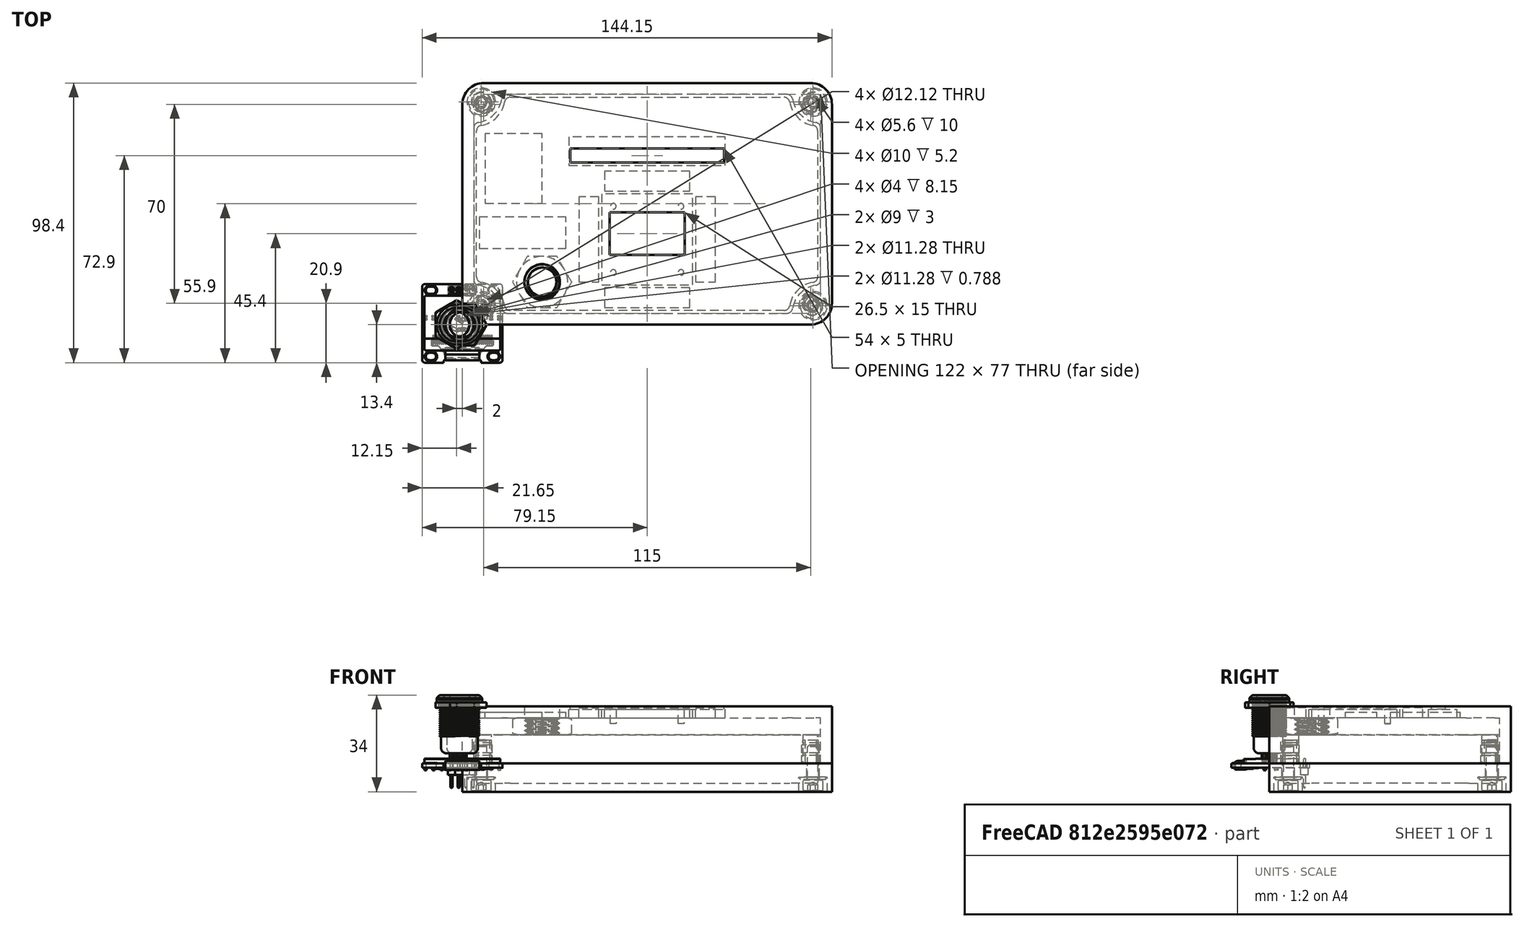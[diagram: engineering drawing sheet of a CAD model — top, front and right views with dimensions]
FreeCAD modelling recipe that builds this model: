
FCSTD DOCUMENT  (FreeCAD 0.20R27319 (Git))
Label: FirstDraft
License: All rights reserved
LicenseURL: http://en.wikipedia.org/wiki/All_rights_reserved
objects: Part::Feature×49, Part::FeaturePython×14, Sketcher::SketchObject×12, App::Part×10, PartDesign::Pocket×7, PartDesign::CoordinateSystem×4, App::DocumentObjectGroup×4, PartDesign::Line×4, PartDesign::Pad×3, App::Link×2, PartDesign::Body×2, PartDesign::AdditiveBox×1, Mesh::Feature×1, App::FeaturePython×1, PartDesign::Fillet×1, PartDesign::ShapeBinder×1, PartDesign::Hole×1
note: 112 computed .brp shape members not serialized (recipe doc carries the construction recipe); baked Part::Feature solids carry a one-line shape summary decoded from their .brp

FEATURE [PartDesign::AdditiveBox] Box002
  AttacherType = Attacher::AttachEngine3D
  Height = 20
  Length = 130
  Width = 85
FEATURE [Sketcher::SketchObject] Sketch001
  ExternalGeometry = -> [Box002]
  FullyConstrained = true
  MapMode = 5
  Placement = pos=(0,0,0) rot=(1,0,0;3.14159rad)
  Support = -> [Box002]
  sketch-geometry (23):
    g0: LineSegment StartX=15.8322 StartY=-4 StartZ=0 EndX=114.168 EndY=-4 EndZ=0
    g1: LineSegment StartX=126 StartY=-15.8322 StartZ=0 EndX=126 EndY=-69.1678 EndZ=0
    g2: LineSegment StartX=114.168 StartY=-81 StartZ=0 EndX=15.8322 EndY=-81 EndZ=0
    g3: LineSegment StartX=4 StartY=-69.1678 StartZ=0 EndX=4 EndY=-15.8322 EndZ=0
    g4: GeomPoint X=4 Y=-4 Z=0
    g5: GeomPoint X=126 Y=-81 Z=0
    g6: GeomPoint X=65 Y=-42.5 Z=0
    g7: ArcOfCircle CenterX=4 CenterY=-81 CenterZ=0 NormalX=0 NormalY=0 NormalZ=1 AngleXU=0 Radius=10 StartAngle=0.167448 EndAngle=1.40335
    g8: ArcOfCircle CenterX=6 CenterY=-69.1678 CenterZ=0 NormalX=0 NormalY=0 NormalZ=1 AngleXU=0 Radius=2 StartAngle=3.14159 EndAngle=4.54494
    g9: ArcOfCircle CenterX=15.8322 CenterY=-79 CenterZ=0 NormalX=0 NormalY=0 NormalZ=1 AngleXU=0 Radius=2 StartAngle=3.30904 EndAngle=4.71239
    g10: ArcOfCircle CenterX=4 CenterY=-4 CenterZ=0 NormalX=0 NormalY=0 NormalZ=1 AngleXU=0 Radius=10 StartAngle=4.87984 EndAngle=6.11574
    g11: ArcOfCircle CenterX=126 CenterY=-4 CenterZ=0 NormalX=0 NormalY=0 NormalZ=1 AngleXU=0 Radius=10 StartAngle=3.30904 EndAngle=4.54494
    g12: ArcOfCircle CenterX=126 CenterY=-81 CenterZ=0 NormalX=0 NormalY=0 NormalZ=1 AngleXU=0 Radius=10 StartAngle=1.73824 EndAngle=2.97414
    g13: LineSegment StartX=4 StartY=-81 StartZ=0 EndX=126 EndY=-81 EndZ=0
    g14: LineSegment StartX=126 StartY=-81 StartZ=0 EndX=126 EndY=-4 EndZ=0
    g15: LineSegment StartX=126 StartY=-4 StartZ=0 EndX=4 EndY=-4 EndZ=0
    g16: LineSegment StartX=4 StartY=-4 StartZ=0 EndX=4 EndY=-81 EndZ=0
    g17: ArcOfCircle CenterX=6 CenterY=-15.8322 CenterZ=0 NormalX=0 NormalY=0 NormalZ=1 AngleXU=0 Radius=2 StartAngle=1.73824 EndAngle=3.14159
    g18: ArcOfCircle CenterX=124 CenterY=-15.8322 CenterZ=0 NormalX=0 NormalY=0 NormalZ=1 AngleXU=0 Radius=2 StartAngle=0 EndAngle=1.40335
    g19: ArcOfCircle CenterX=15.8322 CenterY=-6 CenterZ=0 NormalX=0 NormalY=0 NormalZ=1 AngleXU=0 Radius=2 StartAngle=1.5708 EndAngle=2.97414
    g20: ArcOfCircle CenterX=114.168 CenterY=-6 CenterZ=0 NormalX=0 NormalY=0 NormalZ=1 AngleXU=0 Radius=2 StartAngle=0.167448 EndAngle=1.5708
    g21: ArcOfCircle CenterX=124 CenterY=-69.1678 CenterZ=0 NormalX=0 NormalY=0 NormalZ=1 AngleXU=0 Radius=2 StartAngle=4.87984 EndAngle=6.28319
    g22: ArcOfCircle CenterX=114.168 CenterY=-79 CenterZ=0 NormalX=0 NormalY=0 NormalZ=1 AngleXU=0 Radius=2 StartAngle=4.71239 EndAngle=6.11574
  constraints (56):
    c: Horizontal(g0)
    c: Horizontal(g2)
    c: Vertical(g1)
    c: Vertical(g3)
    c: PointOnObject(g4,g0)
    c: PointOnObject(g4,g3)
    c: PointOnObject(g5,g1)
    c: PointOnObject(g5,g2)
    c: Symmetric(g-6,g-4,g6)
    c: Tangent(g7,g8) = 1.5708
    c: Tangent(g3,g8) = 1.5708
    c: Tangent(g2,g9) = 1.5708
    c: Tangent(g7,g9) = 1.5708
    c: Coincident(g12,g5)
    c: Coincident(g13,g14)
    c: Coincident(g14,g15)
    c: Coincident(g15,g16)
    c: Coincident(g16,g13)
    c: Horizontal(g13)
    c: Horizontal(g15)
    c: Vertical(g14)
    c: Vertical(g16)
    c: Coincident(g13,g7)
    c: Coincident(g14,g11)
    c: Coincident(g4,g10)
    c: Symmetric(g7,g11,g6)
    c: Tangent(g3,g17) = 1.5708
    c: Tangent(g10,g17) = 1.5708
    c: Tangent(g1,g18) = 1.5708
    c: Tangent(g11,g18) = 1.5708
    c: Tangent(g10,g19) = 1.5708
    c: Tangent(g0,g19) = 1.5708
    c: Tangent(g11,g20) = 1.5708
    c: Tangent(g0,g20) = 1.5708
    c: Tangent(g1,g21) = 1.5708
    c: Tangent(g12,g21) = 1.5708
    c: Tangent(g2,g22) = 1.5708
    c: Tangent(g12,g22) = 1.5708
    c: PointOnObject(g0,g15)
    c: PointOnObject(g3,g16)
    c: PointOnObject(g1,g14)
    c: DistanceX(g-6,g7) = 4
    c: DistanceY(g-6,g7) = 4
    c: PointOnObject(g2,g13)
    c: Equal(g7,g10)
    c: Equal(g10,g11)
    c: Equal(g11,g12)
    c: Radius(g7) = 10
    c: Equal(g9,g8)
    c: Equal(g8,g19)
    c: Equal(g19,g17)
    c: Equal(g17,g20)
    c: Equal(g20,g18)
    c: Equal(g18,g21)
    c: Equal(g21,g22)
    c: Radius(g9) = 2
FEATURE [PartDesign::Pocket] Pocket001
  BaseFeature = -> Box002
  Direction = (0,0,1)
  Length = 16
  Length2 = 100
  Profile = -> Sketch001
  ReferenceAxis = -> Sketch001 [N_Axis]
  Type = 0
  expr: Length = <<Box002>>.Height - 4mm
FEATURE [Sketcher::SketchObject] Sketch002
  ExternalGeometry = -> [Pocket001]
  FullyConstrained = true
  MapMode = 5
  Placement = pos=(0,0,16) rot=(1,0,0;3.14159rad)
  Support = -> [Pocket001]
  sketch-geometry (11):
    g0: LineSegment StartX=49 StartY=-14 StartZ=0 EndX=81 EndY=-14 EndZ=0
    g1: LineSegment StartX=81 StartY=-14 StartZ=0 EndX=81 EndY=-46 EndZ=0
    g2: LineSegment StartX=81 StartY=-46 StartZ=0 EndX=49 EndY=-46 EndZ=0
    g3: LineSegment StartX=49 StartY=-46 StartZ=0 EndX=49 EndY=-14 EndZ=0
    g4: GeomPoint X=65 Y=-4 Z=0
    g5: LineSegment StartX=65 StartY=-4 StartZ=0 EndX=65 EndY=-14 EndZ=0
    g6: LineSegment StartX=37.5 StartY=-56 StartZ=0 EndX=92.5 EndY=-56 EndZ=0
    g7: LineSegment StartX=92.5 StartY=-56 StartZ=0 EndX=92.5 EndY=-66 EndZ=0
    g8: LineSegment StartX=92.5 StartY=-66 StartZ=0 EndX=37.5 EndY=-66 EndZ=0
    g9: LineSegment StartX=37.5 StartY=-66 StartZ=0 EndX=37.5 EndY=-56 EndZ=0
    g10: LineSegment StartX=65 StartY=-14 StartZ=0 EndX=65 EndY=-56 EndZ=0
  constraints (29):
    c: Coincident(g0,g1)
    c: Coincident(g1,g2)
    c: Coincident(g2,g3)
    c: Coincident(g3,g0)
    c: Horizontal(g0)
    c: Horizontal(g2)
    c: Vertical(g1)
    c: Vertical(g3)
    c: Coincident(g5,g4)
    c: Vertical(g5)
    c: Symmetric(g0,g0,g5)
    c: DistanceY(g5,g5) = 10
    c: DistanceY(g1,g1) = 32
    c: Equal(g1,g0)
    c: Coincident(g6,g7)
    c: Coincident(g7,g8)
    c: Coincident(g8,g9)
    c: Coincident(g9,g6)
    c: Horizontal(g6)
    c: Horizontal(g8)
    c: Vertical(g7)
    c: Vertical(g9)
    c: DistanceX(g6,g6) = 55
    c: DistanceY(g7,g7) = 10
    c: Coincident(g10,g5)
    c: Vertical(g10)
    c: Symmetric(g6,g6,g10)
    c: DistanceY(g6,g1) = 10
    c: Symmetric(g-3,g-3,g4)
FEATURE [PartDesign::Pocket] Pocket002  label="Platz OLED und LED-Strip"
  BaseFeature = -> Pocket001
  Direction = (0,0,1)
  Length = 3
  Length2 = 100
  Profile = -> Sketch002
  Type = 0
FEATURE [Sketcher::SketchObject] Sketch003
  ExternalGeometry = -> [Sketch002,Pocket002]
  FullyConstrained = true
  MapMode = 5
  Placement = pos=(0,0,16) rot=(1,0,0;3.14159rad)
  Support = -> [Pocket002]
  sketch-geometry (10):
    g0: LineSegment StartX=51.75 StartY=-24.5 StartZ=0 EndX=78.25 EndY=-24.5 EndZ=0
    g1: LineSegment StartX=78.25 StartY=-24.5 StartZ=0 EndX=78.25 EndY=-39.5 EndZ=0
    g2: LineSegment StartX=78.25 StartY=-39.5 StartZ=0 EndX=51.75 EndY=-39.5 EndZ=0
    g3: LineSegment StartX=51.75 StartY=-39.5 StartZ=0 EndX=51.75 EndY=-24.5 EndZ=0
    g4: LineSegment StartX=38 StartY=-57 StartZ=0 EndX=92 EndY=-57 EndZ=0
    g5: LineSegment StartX=92 StartY=-57 StartZ=0 EndX=92 EndY=-62 EndZ=0
    g6: LineSegment StartX=92 StartY=-62 StartZ=0 EndX=38 EndY=-62 EndZ=0
    g7: LineSegment StartX=38 StartY=-62 StartZ=0 EndX=38 EndY=-57 EndZ=0
    g8: LineSegment StartX=65 StartY=-57 StartZ=0 EndX=65 EndY=-56 EndZ=0
    g9: LineSegment StartX=65 StartY=-24.5 StartZ=0 EndX=65 EndY=-14 EndZ=0
  constraints (28):
    c: Coincident(g0,g1)
    c: Coincident(g1,g2)
    c: Coincident(g2,g3)
    c: Coincident(g3,g0)
    c: Horizontal(g0)
    c: Horizontal(g2)
    c: Vertical(g1)
    c: Vertical(g3)
    c: DistanceX(g0,g0) = 26.5
    c: DistanceY(g1,g1) = 15
    c: Coincident(g4,g5)
    c: Coincident(g5,g6)
    c: Coincident(g6,g7)
    c: Coincident(g7,g4)
    c: Horizontal(g4)
    c: Horizontal(g6)
    c: Vertical(g5)
    c: Vertical(g7)
    c: DistanceX(g4,g-3) = 0.5
    c: Vertical(g8)
    c: Symmetric(g4,g4,g8)
    c: Symmetric(g-3,g-4,g8)
    c: DistanceY(g5,g5) = 5
    c: DistanceY(g4,g-3) = 1
    c: Vertical(g9)
    c: Symmetric(g0,g0,g9)
    c: DistanceY(g9,g9) = 10.5
    c: Symmetric(g-5,g-5,g9)
FEATURE [PartDesign::Pocket] Pocket003  label="Sichtausschnitt"
  BaseFeature = -> Pocket002
  Direction = (0,0,1)
  Length = 1.01
  Length2 = 100
  Profile = -> Sketch003
  ReferenceAxis = -> Sketch003 [N_Axis]
  Type = 1
FEATURE [Sketcher::SketchObject] Sketch004  label="Sketch Halter OLED"
  ExternalGeometry = -> [Sketch002]
  FullyConstrained = true
  MapMode = 5
  Placement = pos=(0,0,19) rot=(1,0,0;3.14159rad)
  Support = -> [Pocket003]
  sketch-geometry (9):
    g0: Circle CenterX=53.1 CenterY=-18.35 CenterZ=0 NormalX=0 NormalY=0 NormalZ=1 AngleXU=0 Radius=1
    g1: Circle CenterX=76.9 CenterY=-18.35 CenterZ=0 NormalX=0 NormalY=0 NormalZ=1 AngleXU=0 Radius=1
    g2: Circle CenterX=76.9 CenterY=-41.65 CenterZ=0 NormalX=0 NormalY=0 NormalZ=1 AngleXU=0 Radius=1
    g3: Circle CenterX=53.1 CenterY=-41.65 CenterZ=0 NormalX=0 NormalY=0 NormalZ=1 AngleXU=0 Radius=1
    g4: LineSegment StartX=53.1 StartY=-18.35 StartZ=0 EndX=76.9 EndY=-18.35 EndZ=0
    g5: LineSegment StartX=76.9 StartY=-18.35 StartZ=0 EndX=76.9 EndY=-41.65 EndZ=0
    g6: LineSegment StartX=76.9 StartY=-41.65 StartZ=0 EndX=53.1 EndY=-41.65 EndZ=0
    g7: LineSegment StartX=53.1 StartY=-41.65 StartZ=0 EndX=53.1 EndY=-18.35 EndZ=0
    g8: GeomPoint X=65 Y=-30 Z=0
  constraints (20):
    c: Coincident(g4,g5)
    c: Coincident(g5,g6)
    c: Coincident(g6,g7)
    c: Coincident(g7,g4)
    c: Horizontal(g4)
    c: Horizontal(g6)
    c: Vertical(g5)
    c: Vertical(g7)
    c: Coincident(g4,g0)
    c: Coincident(g5,g2)
    c: Coincident(g1,g4)
    c: Coincident(g3,g6)
    c: Equal(g0,g1)
    c: Equal(g1,g2)
    c: Equal(g2,g3)
    c: Diameter(g1) = 2
    c: DistanceX(g4,g4) = 23.8
    c: DistanceY(g5,g5) = 23.3
    c: Symmetric(g-4,g-6,g8)
    c: Symmetric(g3,g1,g8)
FEATURE [PartDesign::Pad] Pad  label="Halter OLED"
  BaseFeature = -> Pocket003
  Direction = (0,0,-1)
  Length = 5
  Length2 = 100
  Profile = -> Sketch004
  ReferenceAxis = -> Sketch004 [N_Axis]
  Type = 0
FEATURE [Sketcher::SketchObject] Sketch005
  ExternalGeometry = -> [Sketch002]
  FullyConstrained = true
  MapMode = 5
  Placement = pos=(0,0,16) rot=(1,0,0;3.14159rad)
  Support = -> [Pad]
  sketch-geometry (26):
    g0: LineSegment StartX=50 StartY=-6 StartZ=0 EndX=80 EndY=-6 EndZ=0
    g1: LineSegment StartX=80 StartY=-6 StartZ=0 EndX=80 EndY=-13 EndZ=0
    g2: LineSegment StartX=80 StartY=-13 StartZ=0 EndX=50 EndY=-13 EndZ=0
    g3: LineSegment StartX=50 StartY=-13 StartZ=0 EndX=50 EndY=-6 EndZ=0
    g4: LineSegment StartX=82 StartY=-15 StartZ=0 EndX=89 EndY=-15 EndZ=0
    g5: LineSegment StartX=89 StartY=-15 StartZ=0 EndX=89 EndY=-45 EndZ=0
    g6: LineSegment StartX=89 StartY=-45 StartZ=0 EndX=82 EndY=-45 EndZ=0
    g7: LineSegment StartX=82 StartY=-45 StartZ=0 EndX=82 EndY=-15 EndZ=0
    g8: LineSegment StartX=41 StartY=-15 StartZ=0 EndX=48 EndY=-15 EndZ=0
    g9: LineSegment StartX=48 StartY=-15 StartZ=0 EndX=48 EndY=-45 EndZ=0
    g10: LineSegment StartX=48 StartY=-45 StartZ=0 EndX=41 EndY=-45 EndZ=0
    g11: LineSegment StartX=41 StartY=-45 StartZ=0 EndX=41 EndY=-15 EndZ=0
    g12: LineSegment StartX=50 StartY=-47 StartZ=0 EndX=80 EndY=-47 EndZ=0
    g13: LineSegment StartX=80 StartY=-47 StartZ=0 EndX=80 EndY=-54 EndZ=0
    g14: LineSegment StartX=80 StartY=-54 StartZ=0 EndX=50 EndY=-54 EndZ=0
    g15: LineSegment StartX=50 StartY=-54 StartZ=0 EndX=50 EndY=-47 EndZ=0
    g16: LineSegment StartX=48 StartY=-13 StartZ=0 EndX=82 EndY=-13 EndZ=0
    g17: LineSegment StartX=82 StartY=-13 StartZ=0 EndX=82 EndY=-47 EndZ=0
    g18: LineSegment StartX=82 StartY=-47 StartZ=0 EndX=48 EndY=-47 EndZ=0
    g19: LineSegment StartX=48 StartY=-47 StartZ=0 EndX=48 EndY=-13 EndZ=0
    g20: GeomPoint X=65 Y=-30 Z=0
    g21: GeomPoint X=48 Y=-30 Z=0
    g22: GeomPoint X=116 Y=-13 Z=0
    g23: GeomPoint X=82 Y=-30 Z=0
    g24: GeomPoint X=65 Y=-47 Z=0
    g25: GeomPoint X=65 Y=-13 Z=0
  constraints (61):
    c: Coincident(g0,g1)
    c: Coincident(g1,g2)
    c: Coincident(g2,g3)
    c: Coincident(g3,g0)
    c: Horizontal(g0)
    c: Horizontal(g2)
    c: Vertical(g1)
    c: Vertical(g3)
    c: Coincident(g4,g5)
    c: Coincident(g5,g6)
    c: Coincident(g6,g7)
    c: Coincident(g7,g4)
    c: Horizontal(g4)
    c: Horizontal(g6)
    c: Vertical(g5)
    c: Vertical(g7)
    c: Coincident(g8,g9)
    c: Coincident(g9,g10)
    c: Coincident(g10,g11)
    c: Coincident(g11,g8)
    c: Horizontal(g8)
    c: Horizontal(g10)
    c: Vertical(g9)
    c: Vertical(g11)
    c: Coincident(g12,g13)
    c: Coincident(g13,g14)
    c: Coincident(g14,g15)
    c: Coincident(g15,g12)
    c: Horizontal(g12)
    c: Horizontal(g14)
    c: Vertical(g13)
    c: Vertical(g15)
    c: Equal(g4,g1)
    c: Equal(g1,g8)
    c: Equal(g8,g13)
    c: Coincident(g16,g17)
    c: Coincident(g17,g18)
    c: Coincident(g18,g19)
    c: Coincident(g19,g16)
    c: DistanceX(g-4,g16) = 1
    c: DistanceY(g-4,g16) = 1
    c: Symmetric(g16,g18,g20)
    c: Symmetric(g-6,g-4,g20)
    c: DistanceY(g15,g15) = 7
    c: Vertical(g19)
    c: Horizontal(g16)
    c: PointOnObject(g12,g18)
    c: Vertical(g17)
    c: Equal(g0,g11)
    c: Equal(g11,g5)
    c: Equal(g5,g14)
    c: DistanceY(g11,g11) = 30
    c: Symmetric(g18,g17,g24)
    c: Symmetric(g6,g4,g23)
    c: Symmetric(g16,g22,g16)
    c: Symmetric(g16,g18,g21)
    c: Symmetric(g8,g9,g21)
    c: Symmetric(g17,g16,g23)
    c: Symmetric(g12,g12,g24)
    c: Symmetric(g2,g1,g25)
    c: Symmetric(g16,g16,g25)
FEATURE [PartDesign::Pocket] Pocket004  label="Ausschnitte  Touch"
  BaseFeature = -> Pad
  Direction = (0,0,1)
  Length = 3.5
  Length2 = 100
  Profile = -> Sketch005
  Type = 0
FEATURE [Part::Feature] Part__Feature  label="Pantalla"
  Placement = pos=(4e-15,0.525,-1e-15) rot=(0,0,1;0rad)
  shape: bbox 26.68 x 19.2 x 1.6 mm, 12 faces (baked)
FEATURE [Part::Feature] Part__Feature001  label="PADS"
  shape: bbox 0.4 x 3 x 0.1 mm, 6 faces (baked)
FEATURE [Part::Feature] Part__Feature002  label="PADS001"
  shape: bbox 0.4 x 3 x 0.1 mm, 6 faces (baked)
FEATURE [Part::Feature] Part__Feature003  label="PADS002"
  shape: bbox 0.4 x 3 x 0.1 mm, 6 faces (baked)
FEATURE [Part::Feature] Part__Feature004  label="PADS003"
  shape: bbox 0.4 x 3 x 0.1 mm, 6 faces (baked)
FEATURE [Part::Feature] Part__Feature005  label="PADS004"
  shape: bbox 0.4 x 3 x 0.1 mm, 6 faces (baked)
FEATURE [Part::Feature] Part__Feature006  label="PADS005"
  shape: bbox 0.4 x 3 x 0.1 mm, 6 faces (baked)
FEATURE [Part::Feature] Part__Feature007  label="PADS006"
  shape: bbox 0.4 x 3 x 0.1 mm, 6 faces (baked)
FEATURE [Part::Feature] Part__Feature008  label="PADS007"
  shape: bbox 0.4 x 3 x 0.1 mm, 6 faces (baked)
FEATURE [Part::Feature] Part__Feature009  label="PADS008"
  shape: bbox 0.4 x 3 x 0.1 mm, 6 faces (baked)
FEATURE [Part::Feature] Part__Feature010  label="PADS009"
  shape: bbox 0.4 x 3 x 0.1 mm, 6 faces (baked)
FEATURE [Part::Feature] Part__Feature011  label="PADS010"
  shape: bbox 0.4 x 3 x 0.1 mm, 6 faces (baked)
FEATURE [Part::Feature] Part__Feature012  label="PADS011"
  shape: bbox 0.4 x 3 x 0.1 mm, 6 faces (baked)
FEATURE [Part::Feature] Part__Feature013  label="PADS012"
  shape: bbox 0.4 x 3 x 0.1 mm, 6 faces (baked)
FEATURE [Part::Feature] Part__Feature014  label="PADS013"
  shape: bbox 0.4 x 3 x 0.1 mm, 6 faces (baked)
FEATURE [Part::Feature] Part__Feature015  label="PADS014"
  shape: bbox 0.4 x 3 x 0.1 mm, 6 faces (baked)
FEATURE [Part::Feature] Part__Feature016  label="PADS015"
  shape: bbox 0.4 x 3 x 0.1 mm, 6 faces (baked)
FEATURE [Part::Feature] Part__Feature017  label="PADS016"
  shape: bbox 0.4 x 3 x 0.1 mm, 6 faces (baked)
FEATURE [Part::Feature] Part__Feature018  label="PADS017"
  shape: bbox 0.4 x 3 x 0.1 mm, 6 faces (baked)
FEATURE [Part::Feature] Part__Feature019  label="PADS018"
  shape: bbox 0.4 x 3 x 0.1 mm, 6 faces (baked)
FEATURE [Part::Feature] Part__Feature020  label="PADS019"
  shape: bbox 0.4 x 3 x 0.1 mm, 6 faces (baked)
FEATURE [Part::Feature] Part__Feature021  label="PADS020"
  shape: bbox 0.4 x 3 x 0.1 mm, 6 faces (baked)
FEATURE [Part::Feature] Part__Feature022  label="PADS021"
  shape: bbox 0.4 x 3 x 0.1 mm, 6 faces (baked)
FEATURE [Part::Feature] Part__Feature023  label="PADS022"
  shape: bbox 0.4 x 3 x 0.1 mm, 6 faces (baked)
FEATURE [Part::Feature] Part__Feature024  label="PADS023"
  shape: bbox 0.4 x 3 x 0.1 mm, 6 faces (baked)
FEATURE [Part::Feature] Part__Feature025  label="PADS024"
  shape: bbox 0.4 x 3 x 0.1 mm, 6 faces (baked)
FEATURE [Part::Feature] Part__Feature026  label="PADS025"
  shape: bbox 0.4 x 3 x 0.1 mm, 6 faces (baked)
FEATURE [Part::Feature] Part__Feature027  label="PADS026"
  shape: bbox 0.4 x 3 x 0.1 mm, 6 faces (baked)
FEATURE [Part::Feature] Part__Feature028  label="PADS027"
  shape: bbox 0.4 x 3 x 0.1 mm, 6 faces (baked)
FEATURE [Part::Feature] Part__Feature029  label="PADS028"
  shape: bbox 0.4 x 3 x 0.1 mm, 6 faces (baked)
FEATURE [Part::Feature] Part__Feature030  label="PADS029"
  shape: bbox 0.4 x 3 x 0.1 mm, 6 faces (baked)
FEATURE [App::Part] PADS  label="PADS030"
  Group = -> [Part__Feature001,Part__Feature002,Part__Feature003,Part__Feature004,Part__Feature005,Part__Feature006,Part__Feature007,Part__Feature008,Part__Feature009,Part__Feature010,Part__Feature011,Part__Feature012,Part__Feature013,Part__Feature014,Part__Feature015,Part__Feature016,Part__Feature017,Part__Feature018,Part__Feature019,Part__Feature020,Part__Feature021,Part__Feature022,Part__Feature023,+7 more]
  Origin = -> Origin005
FEATURE [Part::Feature] Part__Feature031  label="Base PCB"
  shape: bbox 28.3 x 27.65 x 1.7 mm, 324 faces (baked)
FEATURE [App::Part] Base_PCB  label="Base PCB001"
  Group = -> [PADS,Part__Feature031]
  Origin = -> Origin006
FEATURE [Part::Feature] Part__Feature032  label="PINOS"
  shape: bbox 2.54 x 2.54 x 10.4 mm, 28 faces (baked)
FEATURE [Part::Feature] Part__Feature033  label="PINOS001"
  shape: bbox 2.54 x 2.54 x 10.4 mm, 28 faces (baked)
FEATURE [Part::Feature] Part__Feature034  label="PINOS002"
  shape: bbox 2.54 x 2.54 x 10.4 mm, 28 faces (baked)
FEATURE [Part::Feature] Part__Feature035  label="PINOS003"
  shape: bbox 2.54 x 2.54 x 10.4 mm, 28 faces (baked)
FEATURE [App::Part] PINOS  label="PINOS004"
  Group = -> [Part__Feature032,Part__Feature033,Part__Feature034,Part__Feature035]
  Origin = -> Origin007
FEATURE [Part::Feature] Part__Feature036  label="fLEX"
  Placement = pos=(4e-15,1.525,-0.1) rot=(0,0,1;0rad)
  shape: bbox 39.56 x 36.02 x 13.34 mm, 31 faces (baked)
FEATURE [Part::Feature] Part__Feature037  label="res"
  Placement = pos=(13,2.425,-4) rot=(1,0,0;3.14159rad)
  shape: bbox 1.02 x 1.65 x 0.81 mm, 37 faces (baked)
FEATURE [Part::Feature] Part__Feature038  label="res001"
  Placement = pos=(10.1111,2.425,-4) rot=(1,0,0;3.14159rad)
  shape: bbox 1.02 x 1.65 x 0.81 mm, 37 faces (baked)
FEATURE [Part::Feature] Part__Feature039  label="res002"
  Placement = pos=(7.22222,2.425,-4) rot=(1,0,0;3.14159rad)
  shape: bbox 1.02 x 1.65 x 0.81 mm, 37 faces (baked)
FEATURE [Part::Feature] Part__Feature040  label="res003"
  Placement = pos=(4.33333,2.425,-4) rot=(1,0,0;3.14159rad)
  shape: bbox 1.02 x 1.65 x 0.81 mm, 37 faces (baked)
FEATURE [Part::Feature] Part__Feature041  label="res004"
  Placement = pos=(1.44444,2.425,-4) rot=(1,0,0;3.14159rad)
  shape: bbox 1.02 x 1.65 x 0.81 mm, 37 faces (baked)
FEATURE [Part::Feature] Part__Feature042  label="res005"
  Placement = pos=(-1.44444,2.425,-4) rot=(1,0,0;3.14159rad)
  shape: bbox 1.02 x 1.65 x 0.81 mm, 37 faces (baked)
FEATURE [Part::Feature] Part__Feature043  label="res006"
  Placement = pos=(-4.33333,2.425,-4) rot=(1,0,0;3.14159rad)
  shape: bbox 1.02 x 1.65 x 0.81 mm, 37 faces (baked)
FEATURE [Part::Feature] Part__Feature044  label="res007"
  Placement = pos=(-7.22222,2.425,-4) rot=(1,0,0;3.14159rad)
  shape: bbox 1.02 x 1.65 x 0.81 mm, 37 faces (baked)
FEATURE [Part::Feature] Part__Feature045  label="res008"
  Placement = pos=(-10.1111,2.425,-4) rot=(1,0,0;3.14159rad)
  shape: bbox 1.02 x 1.65 x 0.81 mm, 37 faces (baked)
FEATURE [Part::Feature] Part__Feature046  label="res009"
  Placement = pos=(-13,2.425,-4) rot=(1,0,0;3.14159rad)
  shape: bbox 1.02 x 1.65 x 0.81 mm, 37 faces (baked)
FEATURE [Part::Feature] Part__Feature047  label="res010"
  Placement = pos=(0,-1.575,-4) rot=(0.707107,-0.707107,0;3.14159rad)
  shape: bbox 1.65 x 1.02 x 0.81 mm, 37 faces (baked)
FEATURE [App::Part] Resistores_SMD  label="Resistores SMD"
  Group = -> [Part__Feature037,Part__Feature038,Part__Feature039,Part__Feature040,Part__Feature041,Part__Feature042,Part__Feature043,Part__Feature044,Part__Feature045,Part__Feature046,Part__Feature047]
  Origin = -> Origin008
FEATURE [App::Part] Tela_OLed_128x64_v15  label="Tela OLed 128x64 v15"
  Group = -> [Part__Feature,Base_PCB,PINOS,Part__Feature036,Resistores_SMD]
  Origin = -> Origin009
  Placement = pos=(60,29.5,22.5) rot=(0,0,1;0rad)
FEATURE [Mesh::Feature] DuinoPeak_WS2812_RGB_Pixel
FEATURE [Part::Feature] Part__Feature086  label="12mm Switch"
  shape: bbox 17.01 x 15.16 x 24 mm, 165 faces, 3 solids (baked)
FEATURE [App::Part] _2mm_Switch_v5  label="12mm Switch v5"
  Group = -> [Part__Feature086]
  Origin = -> Origin012
  Placement = pos=(15,0,0) rot=(1,0,0;0rad)
FEATURE [Part::FeaturePython] Clone  label="12mm Switch v006"  # Draft clone (typed FeaturePython)
  AttacherType = Attacher::AttachEngine3D
  Fuse = false
  Objects = -> [_2mm_Switch_v5]
  Placement = pos=(-2,-1e-15,0) rot=(0,0,-1;0.523599rad)
  Scale = (1,1,1)
FEATURE [PartDesign::CoordinateSystem] LCS_Origin
  AttacherType = Attacher::AttachEngine3D
  MapMode = 2
  Support = -> [X_Axis013]
FEATURE [App::FeaturePython] Variables  # WARN: FeaturePython — macro-defined, semantics opaque (R4)
  Type = App::PropertyContainer
FEATURE [App::DocumentObjectGroup] Constraints
FEATURE [App::DocumentObjectGroup] Configurations
FEATURE [App::Part] Part  label="Double-Switch"
  Group = -> [Clone,_2mm_Switch_v5]
  Origin = -> Origin014
FEATURE [App::Part] Part001  label="LED-Strip"
  Group = -> [DuinoPeak_WS2812_RGB_Pixel]
  Origin = -> Origin015
  Placement = pos=(34,56,20.6) rot=(0,0,1;0rad)
FEATURE [App::Link] Base  label="Base001"
  AssemblyType = Part::Link
  AttachedBy = #LCS_1
  AttachedTo = Parent Assembly#LCS_Origin
  LinkedObject = -> Body
  SolverId = Asm4EE
  expr: Placement = LCS_Origin.Placement * AttachmentOffset * LCS_1.Placement ^ -1
FEATURE [Part::FeaturePython] HeatSet  label="Auto-HeatSet"  # WARN: FeaturePython — macro-defined, semantics opaque (R4)
  Placement = pos=(7.5,77.5,0) rot=(-1,0,0;3.14159rad)
  baseObject = -> Pocket006 [Edge32]
  diameter = 0
  invert = false
  offset = 0
FEATURE [Part::FeaturePython] HeatSet001  label="Auto-HeatSet001"  # WARN: FeaturePython — macro-defined, semantics opaque (R4)
  Placement = pos=(122.5,77.5,0) rot=(-1,0,0;3.14159rad)
  baseObject = -> Pocket006 [Edge49]
  diameter = 0
  invert = false
  offset = 0
FEATURE [Part::FeaturePython] HeatSet002  label="Auto-HeatSet002"  # WARN: FeaturePython — macro-defined, semantics opaque (R4)
  Placement = pos=(122.5,7.5,0) rot=(-1,0,0;3.14159rad)
  baseObject = -> Pocket006 [Edge31]
  diameter = 0
  invert = false
  offset = 0
FEATURE [Part::FeaturePython] HeatSet003  label="Auto-HeatSet003"  # WARN: FeaturePython — macro-defined, semantics opaque (R4)
  Placement = pos=(7.5,7.5,0) rot=(-1,0,0;3.14159rad)
  baseObject = -> Body002 [Edge30]
  diameter = 0
  invert = false
  offset = 0
FEATURE [App::Link] Front_inkl__Fasteners  label="Front inkl. Fasteners001"
  AssemblyType = Part::Link
  AttachedBy = #LCS_3
  AttachedTo = Base#LCS_1
  LinkedObject = -> Part002
  SolverId = Asm4EE
  expr: Placement = Base.Placement * LCS_1.Placement * AttachmentOffset * LCS_3.Placement ^ -1
FEATURE [Part::FeaturePython] Washer  label="M4-Washer"  # Fasteners workbench fastener (typed FeaturePython)
  Placement = pos=(6.65146,6.65148,-4.8) rot=(-1,0,0;3.14159rad)
  baseObject = -> Body [Edge50]
  diameter = 5
  invert = false
  matchOuter = true
  offset = 0
  type = 3
FEATURE [Part::FeaturePython] Washer001  label="M4-Washer022"  # Fasteners workbench fastener (typed FeaturePython)
  Placement = pos=(123.349,6.65148,-4.8) rot=(-1,0,0;3.14159rad)
  baseObject = -> Body [Edge52]
  diameter = 5
  invert = false
  matchOuter = true
  offset = 0
  type = 3
FEATURE [Part::FeaturePython] Washer002  label="M4-Washer023"  # Fasteners workbench fastener (typed FeaturePython)
  Placement = pos=(123.349,78.3485,-4.8) rot=(-1,0,0;3.14159rad)
  baseObject = -> Body [Edge88]
  diameter = 5
  invert = false
  matchOuter = true
  offset = 0
  type = 3
FEATURE [Part::FeaturePython] Washer003  label="M4-Washer024"  # Fasteners workbench fastener (typed FeaturePython)
  Placement = pos=(6.65146,78.3485,-4.8) rot=(-1,0,0;3.14159rad)
  baseObject = -> Body [Edge54]
  diameter = 5
  invert = false
  matchOuter = true
  offset = 0
  type = 3
FEATURE [Part::FeaturePython] Screw  label="M4x14-Screw"  # Fasteners workbench fastener (typed FeaturePython)
  Placement = pos=(6.65146,78.3485,-5.7) rot=(-1,0,0;3.14159rad)
  baseObject = -> Washer003 [Edge1]
  diameter = 5
  invert = false
  length = 4
  lengthCustom = 14
  matchOuter = false
  offset = 0
  thread = false
  type = 34
FEATURE [Part::FeaturePython] Screw001  label="M4x12-Screw"  # Fasteners workbench fastener (typed FeaturePython)
  Placement = pos=(6.65146,6.65148,-5.7) rot=(-1,0,0;3.14159rad)
  baseObject = -> Washer [Edge1]
  diameter = 5
  invert = false
  length = 3
  lengthCustom = 12
  matchOuter = false
  offset = 0
  thread = false
  type = 34
FEATURE [Part::FeaturePython] Screw002  label="M4x12-Screw013"  # Fasteners workbench fastener (typed FeaturePython)
  Placement = pos=(123.349,6.65148,-5.7) rot=(-1,0,0;3.14159rad)
  baseObject = -> Washer001 [Edge1]
  diameter = 5
  invert = false
  length = 3
  lengthCustom = 12
  matchOuter = false
  offset = 0
  thread = false
  type = 34
FEATURE [Part::FeaturePython] Screw003  label="M4x12-Screw014"  # Fasteners workbench fastener (typed FeaturePython)
  Placement = pos=(123.349,78.3485,-5.7) rot=(-1,0,0;3.14159rad)
  baseObject = -> Washer002 [Edge1]
  diameter = 5
  invert = false
  length = 3
  lengthCustom = 12
  matchOuter = false
  offset = 0
  thread = false
  type = 34
FEATURE [App::DocumentObjectGroup] Fasteners
  Group = -> [Washer,Washer001,Washer002,Washer003,Screw,Screw001,Screw002,Screw003]
FEATURE [App::Part] Assembly
  AssemblyType = Part::Link
  Group = -> [LCS_Origin,Variables,Constraints,Configurations,Base,Front_inkl__Fasteners,Fasteners,Washer,Washer001,Washer002,Washer003,Screw,Screw001,Screw002,Screw003]
  Origin = -> Origin013
  Type = Assembly
FEATURE [PartDesign::Fillet] Fillet
  Base = -> Pocket004 [Edge3,Edge20,Edge6,Edge1]
  BaseFeature = -> Pocket004
  Radius = 7.5
  SupportTransform = false
FEATURE [Sketcher::SketchObject] Sketch
  ExternalGeometry = -> [Fillet]
  FullyConstrained = true
  MapMode = 5
  Placement = pos=(0,0,0) rot=(1,0,0;3.14159rad)
  Support = -> [Fillet]
  sketch-geometry (9):
    g0: LineSegment StartX=7.5 StartY=-7.5 StartZ=0 EndX=122.5 EndY=-7.5 EndZ=0
    g1: LineSegment StartX=122.5 StartY=-7.5 StartZ=0 EndX=122.5 EndY=-77.5 EndZ=0
    g2: LineSegment StartX=122.5 StartY=-77.5 StartZ=0 EndX=7.5 EndY=-77.5 EndZ=0
    g3: LineSegment StartX=7.5 StartY=-77.5 StartZ=0 EndX=7.5 EndY=-7.5 EndZ=0
    g4: GeomPoint X=65 Y=-42.5 Z=0
    g5: Circle CenterX=122.5 CenterY=-7.5 CenterZ=0 NormalX=0 NormalY=0 NormalZ=1 AngleXU=0 Radius=2.8
    g6: Circle CenterX=122.5 CenterY=-77.5 CenterZ=0 NormalX=0 NormalY=0 NormalZ=1 AngleXU=0 Radius=2.8
    g7: Circle CenterX=7.5 CenterY=-77.5 CenterZ=0 NormalX=0 NormalY=0 NormalZ=1 AngleXU=0 Radius=2.8
    g8: Circle CenterX=7.5 CenterY=-7.5 CenterZ=0 NormalX=0 NormalY=0 NormalZ=1 AngleXU=0 Radius=2.8
  constraints (19):
    c: Coincident(g0,g1)
    c: Coincident(g1,g2)
    c: Coincident(g2,g3)
    c: Coincident(g3,g0)
    c: Horizontal(g0)
    c: Horizontal(g2)
    c: Vertical(g1)
    c: Vertical(g3)
    c: Symmetric(g2,g0,g4)
    c: Coincident(g5,g0)
    c: Coincident(g6,g1)
    c: Coincident(g7,g2)
    c: Diameter(g7) = 5.6
    c: Equal(g5,g6)
    c: Equal(g6,g7)
    c: Equal(g7,g8)
    c: Symmetric(g-4,g-5,g4)
    c: Coincident(g0,g8)
    c: Coincident(g8,g-6)
FEATURE [PartDesign::Pocket] Pocket
  BaseFeature = -> Fillet
  Direction = (0,0,1)
  Length = 10
  Length2 = 5
  Profile = -> Sketch
  ReferenceAxis = -> Sketch [N_Axis]
  Type = 0
FEATURE [PartDesign::ShapeBinder] ShapeBinder
  Support = -> [Pocket]
  TraceSupport = true
FEATURE [Sketcher::SketchObject] Sketch010
  ExternalGeometry = -> [ShapeBinder]
  FullyConstrained = true
  MapMode = 5
  Placement = pos=(0,0,0) rot=(1,0,0;3.14159rad)
  Support = -> [ShapeBinder]
  sketch-geometry (23):
    g0: GeomPoint X=5 Y=-5 Z=0
    g1: GeomPoint X=125 Y=-80 Z=0
    g2: GeomPoint X=65 Y=-42.5 Z=0
    g3: ArcOfCircle CenterX=5 CenterY=-80 CenterZ=0 NormalX=0 NormalY=0 NormalZ=1 AngleXU=0 Radius=10 StartAngle=0.167448 EndAngle=1.40335
    g4: ArcOfCircle CenterX=7 CenterY=-68.1678 CenterZ=0 NormalX=0 NormalY=0 NormalZ=1 AngleXU=0 Radius=2 StartAngle=3.14159 EndAngle=4.54494
    g5: ArcOfCircle CenterX=5 CenterY=-5 CenterZ=0 NormalX=0 NormalY=0 NormalZ=1 AngleXU=0 Radius=10 StartAngle=1.40335 EndAngle=6.11574
    g6: ArcOfCircle CenterX=125 CenterY=-5 CenterZ=0 NormalX=0 NormalY=0 NormalZ=1 AngleXU=0 Radius=10 StartAngle=3.30904 EndAngle=4.54494
    g7: ArcOfCircle CenterX=125 CenterY=-80 CenterZ=0 NormalX=0 NormalY=0 NormalZ=1 AngleXU=0 Radius=10 StartAngle=1.73824 EndAngle=2.97414
    g8: LineSegment StartX=5 StartY=-80 StartZ=0 EndX=125 EndY=-80 EndZ=0
    g9: LineSegment StartX=125 StartY=-80 StartZ=0 EndX=125 EndY=-5 EndZ=0
    g10: LineSegment StartX=5 StartY=-5 StartZ=0 EndX=5 EndY=-80 EndZ=0
    g11: ArcOfCircle CenterX=7 CenterY=6.83216 CenterZ=0 NormalX=0 NormalY=0 NormalZ=1 AngleXU=0 Radius=2 StartAngle=4.54494 EndAngle=9.42478
    g12: ArcOfCircle CenterX=123 CenterY=-16.8322 CenterZ=0 NormalX=0 NormalY=0 NormalZ=1 AngleXU=0 Radius=2 StartAngle=4e-16 EndAngle=1.40335
    g13: ArcOfCircle CenterX=16.8322 CenterY=-7 CenterZ=0 NormalX=0 NormalY=0 NormalZ=1 AngleXU=0 Radius=2 StartAngle=1.5708 EndAngle=2.97414
    g14: ArcOfCircle CenterX=113.168 CenterY=-7 CenterZ=0 NormalX=0 NormalY=0 NormalZ=1 AngleXU=0 Radius=2 StartAngle=0.167448 EndAngle=1.5708
    g15: ArcOfCircle CenterX=123 CenterY=-68.1678 CenterZ=0 NormalX=0 NormalY=0 NormalZ=1 AngleXU=0 Radius=2 StartAngle=4.87984 EndAngle=6.28319
    g16: ArcOfCircle CenterX=113.168 CenterY=-78 CenterZ=0 NormalX=0 NormalY=0 NormalZ=1 AngleXU=0 Radius=2 StartAngle=4.71239 EndAngle=6.11574
    g17: ArcOfCircle CenterX=16.8322 CenterY=-78 CenterZ=0 NormalX=0 NormalY=0 NormalZ=1 AngleXU=0 Radius=2 StartAngle=3.30904 EndAngle=4.71239
    g18: LineSegment StartX=5 StartY=-5 StartZ=0 EndX=125 EndY=-5 EndZ=0
    g19: LineSegment StartX=5 StartY=6.83216 StartZ=0 EndX=5 EndY=-68.1678 EndZ=0
    g20: LineSegment StartX=125 StartY=-68.1678 StartZ=0 EndX=125 EndY=-16.8322 EndZ=0
    g21: LineSegment StartX=113.168 StartY=-5 StartZ=0 EndX=16.8322 EndY=-5 EndZ=0
    g22: LineSegment StartX=16.8322 StartY=-80 StartZ=0 EndX=113.168 EndY=-80 EndZ=0
  constraints (54):
    c: Tangent(g3,g4) = 1.5708
    c: Coincident(g7,g1)
    c: Coincident(g8,g9)
    c: Coincident(g10,g8)
    c: Horizontal(g8)
    c: Vertical(g9)
    c: Vertical(g10)
    c: Coincident(g8,g3)
    c: Coincident(g9,g6)
    c: Coincident(g0,g5)
    c: Symmetric(g3,g6,g2)
    c: Tangent(g5,g11) = 1.5708
    c: Tangent(g6,g12) = 1.5708
    c: Tangent(g5,g13) = 1.5708
    c: Tangent(g6,g14) = 1.5708
    c: Tangent(g7,g15) = 1.5708
    c: Tangent(g7,g16) = 1.5708
    c: Equal(g3,g5)
    c: Equal(g5,g6)
    c: Equal(g6,g7)
    c: Radius(g3) = 10
    c: Equal(g4,g13)
    c: Equal(g13,g11)
    c: Equal(g11,g14)
    c: Equal(g12,g15)
    c: Tangent(g16,g8) = -1.5708
    c: Tangent(g4,g10) = -1.5708
    c: Coincident(g8,g7)
    c: Tangent(g17,g8) = -1.5708
    c: Tangent(g17,g3) = 1.5708
    c: Radius(g17) = 2
    c: Tangent(g12,g9) = -1.5708
    c: Tangent(g15,g9) = -1.5708
    c: Tangent(g11,g10) = -1.5708
    c: Coincident(g18,g5)
    c: Horizontal(g18)
    c: Coincident(g18,g6)
    c: Coincident(g10,g5)
    c: Tangent(g13,g18) = 1.5708
    c: Tangent(g14,g18) = 1.5708
    c: Equal(g11,g12)
    c: Equal(g14,g17)
    c: Equal(g17,g16)
    c: Symmetric(g-3,g-5,g2)
    c: Coincident(g19,g11)
    c: Coincident(g19,g4)
    c: Coincident(g20,g15)
    c: Coincident(g20,g12)
    c: Coincident(g21,g14)
    c: Coincident(g21,g13)
    c: DistanceY(g5,g-4) = 1
    c: DistanceX(g-5,g11) = 1
    c: Coincident(g22,g17)
    c: Coincident(g22,g16)
FEATURE [Sketcher::SketchObject] Sketch011
  ExternalGeometry = -> [ShapeBinder]
  FullyConstrained = true
  MapMode = 5
  Placement = pos=(0,0,0) rot=(1,0,0;3.14159rad)
  Support = -> [ShapeBinder]
  sketch-geometry (12):
    g0: LineSegment StartX=7.5 StartY=0 StartZ=0 EndX=122.5 EndY=0 EndZ=0
    g1: LineSegment StartX=130 StartY=-7.5 StartZ=0 EndX=130 EndY=-77.5 EndZ=0
    g2: LineSegment StartX=122.5 StartY=-85 StartZ=0 EndX=7.5 EndY=-85 EndZ=0
    g3: LineSegment StartX=0 StartY=-77.5 StartZ=0 EndX=0 EndY=-7.5 EndZ=0
    g4: ArcOfCircle CenterX=7.5 CenterY=-7.5 CenterZ=0 NormalX=0 NormalY=0 NormalZ=1 AngleXU=0 Radius=7.5 StartAngle=1.5708 EndAngle=3.14159
    g5: GeomPoint X=0 Y=0 Z=0
    g6: ArcOfCircle CenterX=122.5 CenterY=-7.5 CenterZ=0 NormalX=0 NormalY=0 NormalZ=1 AngleXU=0 Radius=7.5 StartAngle=0 EndAngle=1.5708
    g7: GeomPoint X=130 Y=0 Z=0
    g8: ArcOfCircle CenterX=122.5 CenterY=-77.5 CenterZ=0 NormalX=0 NormalY=0 NormalZ=1 AngleXU=0 Radius=7.5 StartAngle=4.71239 EndAngle=6.28319
    g9: GeomPoint X=130 Y=-85 Z=0
    g10: ArcOfCircle CenterX=7.5 CenterY=-77.5 CenterZ=0 NormalX=0 NormalY=0 NormalZ=1 AngleXU=0 Radius=7.5 StartAngle=3.14159 EndAngle=4.71239
    g11: GeomPoint X=0 Y=-85 Z=0
  constraints (23):
    c: Horizontal(g0)
    c: Vertical(g1)
    c: Vertical(g3)
    c: Coincident(g5,g-1)
    c: PointOnObject(g5,g3)
    c: Tangent(g0,g4) = 1.5708
    c: Tangent(g3,g4) = 1.5708
    c: PointOnObject(g7,g1)
    c: PointOnObject(g7,g0)
    c: Tangent(g1,g6) = 1.5708
    c: Tangent(g0,g6) = 1.5708
    c: PointOnObject(g9,g1)
    c: PointOnObject(g9,g2)
    c: Tangent(g1,g8) = 1.5708
    c: Tangent(g2,g8) = 1.5708
    c: PointOnObject(g11,g2)
    c: PointOnObject(g11,g3)
    c: Tangent(g2,g10) = 1.5708
    c: Tangent(g3,g10) = 1.5708
    c: Coincident(g2,g-4)
    c: Coincident(g2,g-4)
    c: Coincident(g-3,g1)
    c: Coincident(g0,g-5)
FEATURE [PartDesign::Pad] Pad003
  Direction = (0,0,-1)
  Length = 10
  Length2 = 10
  Profile = -> Sketch011
  ReferenceAxis = -> Sketch011 [N_Axis]
  Type = 0
FEATURE [PartDesign::Pocket] Pocket005
  BaseFeature = -> Pad003
  Direction = (0,0,1)
  Length = 7
  Length2 = 5
  Profile = -> Sketch010
  ReferenceAxis = -> Sketch010 [N_Axis]
  Reversed = true
  Type = 0
FEATURE [Sketcher::SketchObject] Sketch012
  ExternalGeometry = -> [ShapeBinder]
  FullyConstrained = true
  MapMode = 5
  Placement = pos=(0,0,-10) rot=(1,0,0;3.14159rad)
  Support = -> [Pocket005]
  sketch-geometry (4):
    g0: Circle CenterX=6.65146 CenterY=-6.65148 CenterZ=0 NormalX=0 NormalY=0 NormalZ=1 AngleXU=0 Radius=2.8
    g1: Circle CenterX=123.349 CenterY=-6.65148 CenterZ=0 NormalX=0 NormalY=0 NormalZ=1 AngleXU=0 Radius=2.8
    g2: Circle CenterX=123.349 CenterY=-78.3485 CenterZ=0 NormalX=0 NormalY=0 NormalZ=1 AngleXU=0 Radius=2.8
    g3: Circle CenterX=6.65146 CenterY=-78.3485 CenterZ=0 NormalX=0 NormalY=0 NormalZ=1 AngleXU=0 Radius=2.8
  constraints (8):
    c: Coincident(g1,g-4)
    c: Coincident(g2,g-5)
    c: Coincident(g3,g-6)
    c: Coincident(g0,g-3)
    c: Equal(g0,g-3)
    c: Equal(g0,g1)
    c: Equal(g1,g2)
    c: Equal(g2,g3)
FEATURE [PartDesign::Hole] Hole
  BaseFeature = -> Pocket005
  CustomThreadClearance = 0
  Depth = 314.401
  DepthType = 1
  Diameter = 4.5
  DrillForDepth = false
  DrillPoint = 1
  DrillPointAngle = 118
  HoleCutCountersinkAngle = 90
  HoleCutCustomValues = false
  HoleCutDepth = 5.2
  HoleCutDiameter = 10
  HoleCutType = 12
  ModelThread = false
  Profile = -> Sketch012
  Tapered = false
  TaperedAngle = 90
  ThreadClass = 0
  ThreadDepth = 314.401
  ThreadDepthType = 0
  ThreadDirection = 0
  ThreadFit = 0
  ThreadSize = 11
  ThreadType = 1
  Threaded = false
  UseCustomThreadClearance = false
FEATURE [Sketcher::SketchObject] Sketch013
  ExternalGeometry = -> [ShapeBinder]
  FullyConstrained = true
  MapMode = 5
  Placement = pos=(0,0,0) rot=(1,0,0;3.14159rad)
  Support = -> [ShapeBinder]
  sketch-geometry (46):
    g0: GeomPoint X=5 Y=-28.6643 Z=0
    g1: GeomPoint X=125 Y=-80 Z=0
    g2: GeomPoint X=65 Y=-54.3322 Z=0
    g3: ArcOfCircle CenterX=5 CenterY=-80 CenterZ=0 NormalX=0 NormalY=0 NormalZ=1 AngleXU=0 Radius=10 StartAngle=0.167448 EndAngle=1.40335
    g4: ArcOfCircle CenterX=7 CenterY=-68.1678 CenterZ=0 NormalX=0 NormalY=0 NormalZ=1 AngleXU=0 Radius=2 StartAngle=3.14159 EndAngle=4.54494
    g5: ArcOfCircle CenterX=5 CenterY=-28.6643 CenterZ=0 NormalX=0 NormalY=0 NormalZ=1 AngleXU=0 Radius=10 StartAngle=4.87984 EndAngle=6.11574
    g6: ArcOfCircle CenterX=125 CenterY=-28.6643 CenterZ=0 NormalX=0 NormalY=0 NormalZ=1 AngleXU=0 Radius=10 StartAngle=3.30904 EndAngle=4.54494
    g7: ArcOfCircle CenterX=125 CenterY=-80 CenterZ=0 NormalX=0 NormalY=0 NormalZ=1 AngleXU=0 Radius=10 StartAngle=1.73824 EndAngle=2.97414
    g8: LineSegment StartX=5 StartY=-80 StartZ=0 EndX=125 EndY=-80 EndZ=0
    g9: LineSegment StartX=125 StartY=-80 StartZ=0 EndX=125 EndY=-28.6643 EndZ=0
    g10: LineSegment StartX=5 StartY=-28.6643 StartZ=0 EndX=5 EndY=-80 EndZ=0
    g11: ArcOfCircle CenterX=7 CenterY=-40.4965 CenterZ=0 NormalX=0 NormalY=0 NormalZ=1 AngleXU=0 Radius=2 StartAngle=1.73824 EndAngle=3.14159
    g12: ArcOfCircle CenterX=123 CenterY=-40.4965 CenterZ=0 NormalX=0 NormalY=0 NormalZ=1 AngleXU=0 Radius=2 StartAngle=-9e-16 EndAngle=1.40335
    g13: ArcOfCircle CenterX=16.8322 CenterY=-30.6643 CenterZ=0 NormalX=0 NormalY=0 NormalZ=1 AngleXU=0 Radius=2 StartAngle=1.5708 EndAngle=2.97414
    g14: ArcOfCircle CenterX=113.168 CenterY=-30.6643 CenterZ=0 NormalX=0 NormalY=0 NormalZ=1 AngleXU=0 Radius=2 StartAngle=0.167448 EndAngle=1.5708
    g15: ArcOfCircle CenterX=123 CenterY=-68.1678 CenterZ=0 NormalX=0 NormalY=0 NormalZ=1 AngleXU=0 Radius=2 StartAngle=4.87984 EndAngle=6.28319
    g16: ArcOfCircle CenterX=113.168 CenterY=-78 CenterZ=0 NormalX=0 NormalY=0 NormalZ=1 AngleXU=0 Radius=2 StartAngle=4.71239 EndAngle=6.11574
    g17: ArcOfCircle CenterX=16.8322 CenterY=-78 CenterZ=0 NormalX=0 NormalY=0 NormalZ=1 AngleXU=0 Radius=2 StartAngle=3.30904 EndAngle=4.71239
    g18: LineSegment StartX=5 StartY=-28.6643 StartZ=0 EndX=125 EndY=-28.6643 EndZ=0
    g19: LineSegment StartX=5 StartY=-40.4965 StartZ=0 EndX=5 EndY=-68.1678 EndZ=0
    g20: LineSegment StartX=125 StartY=-68.1678 StartZ=0 EndX=125 EndY=-40.4965 EndZ=0
    g21: LineSegment StartX=113.168 StartY=-28.6643 StartZ=0 EndX=16.8322 EndY=-28.6643 EndZ=0
    g22: LineSegment StartX=16.8322 StartY=-80 StartZ=0 EndX=113.168 EndY=-80 EndZ=0
    g23: GeomPoint X=4 Y=-27.6643 Z=0
    g24: GeomPoint X=126 Y=-81 Z=0
    g25: GeomPoint X=65 Y=-54.3322 Z=0
    g26: ArcOfCircle CenterX=4 CenterY=-81 CenterZ=0 NormalX=0 NormalY=0 NormalZ=1 AngleXU=0 Radius=10 StartAngle=0.167448 EndAngle=1.40335
    g27: ArcOfCircle CenterX=6 CenterY=-69.1678 CenterZ=0 NormalX=0 NormalY=0 NormalZ=1 AngleXU=0 Radius=2 StartAngle=3.14159 EndAngle=4.54494
    g28: ArcOfCircle CenterX=4 CenterY=-27.6643 CenterZ=0 NormalX=0 NormalY=0 NormalZ=1 AngleXU=0 Radius=10 StartAngle=1.40335 EndAngle=6.11574
    g29: ArcOfCircle CenterX=126 CenterY=-27.6643 CenterZ=0 NormalX=0 NormalY=0 NormalZ=1 AngleXU=0 Radius=10 StartAngle=3.30904 EndAngle=4.54494
    g30: ArcOfCircle CenterX=126 CenterY=-81 CenterZ=0 NormalX=0 NormalY=0 NormalZ=1 AngleXU=0 Radius=10 StartAngle=1.73824 EndAngle=2.97414
    g31: LineSegment StartX=4 StartY=-81 StartZ=0 EndX=126 EndY=-81 EndZ=0
    g32: LineSegment StartX=126 StartY=-81 StartZ=0 EndX=126 EndY=-27.6643 EndZ=0
    g33: LineSegment StartX=4 StartY=-27.6643 StartZ=0 EndX=4 EndY=-81 EndZ=0
    g34: ArcOfCircle CenterX=6 CenterY=-15.8322 CenterZ=0 NormalX=0 NormalY=0 NormalZ=1 AngleXU=0 Radius=2 StartAngle=4.54494 EndAngle=9.42478
    g35: ArcOfCircle CenterX=124 CenterY=-39.4965 CenterZ=0 NormalX=0 NormalY=0 NormalZ=1 AngleXU=0 Radius=2 StartAngle=-9e-16 EndAngle=1.40335
    g36: ArcOfCircle CenterX=15.8322 CenterY=-29.6643 CenterZ=0 NormalX=0 NormalY=0 NormalZ=1 AngleXU=0 Radius=2 StartAngle=1.5708 EndAngle=2.97414
    g37: ArcOfCircle CenterX=114.168 CenterY=-29.6643 CenterZ=0 NormalX=0 NormalY=0 NormalZ=1 AngleXU=0 Radius=2 StartAngle=0.167448 EndAngle=1.5708
    g38: ArcOfCircle CenterX=124 CenterY=-69.1678 CenterZ=0 NormalX=0 NormalY=0 NormalZ=1 AngleXU=0 Radius=2 StartAngle=4.87984 EndAngle=6.28319
    g39: ArcOfCircle CenterX=114.168 CenterY=-79 CenterZ=0 NormalX=0 NormalY=0 NormalZ=1 AngleXU=0 Radius=2 StartAngle=4.71239 EndAngle=6.11574
    g40: ArcOfCircle CenterX=15.8322 CenterY=-79 CenterZ=0 NormalX=0 NormalY=0 NormalZ=1 AngleXU=0 Radius=2 StartAngle=3.30904 EndAngle=4.71239
    g41: LineSegment StartX=4 StartY=-27.6643 StartZ=0 EndX=126 EndY=-27.6643 EndZ=0
    g42: LineSegment StartX=4 StartY=-15.8322 StartZ=0 EndX=4 EndY=-69.1678 EndZ=0
    g43: LineSegment StartX=126 StartY=-69.1678 StartZ=0 EndX=126 EndY=-39.4965 EndZ=0
    g44: LineSegment StartX=114.168 StartY=-27.6643 StartZ=0 EndX=15.8322 EndY=-27.6643 EndZ=0
    g45: LineSegment StartX=15.8322 StartY=-81 StartZ=0 EndX=114.168 EndY=-81 EndZ=0
  constraints (107):
    c: Tangent(g3,g4) = 1.5708
    c: Coincident(g7,g1)
    c: Coincident(g8,g9)
    c: Coincident(g10,g8)
    c: Horizontal(g8)
    c: Vertical(g9)
    c: Vertical(g10)
    c: Coincident(g8,g3)
    c: Coincident(g9,g6)
    c: Coincident(g0,g5)
    c: Symmetric(g3,g6,g2)
    c: Tangent(g5,g11) = 1.5708
    c: Tangent(g6,g12) = 1.5708
    c: Tangent(g5,g13) = 1.5708
    c: Tangent(g6,g14) = 1.5708
    c: Tangent(g7,g15) = 1.5708
    c: Tangent(g7,g16) = 1.5708
    c: Equal(g3,g5)
    c: Equal(g5,g6)
    c: Equal(g6,g7)
    c: Radius(g3) = 10
    c: Equal(g4,g13)
    c: Equal(g13,g11)
    c: Equal(g11,g14)
    c: Equal(g12,g15)
    c: Tangent(g16,g8) = -1.5708
    c: Tangent(g4,g10) = -1.5708
    c: Coincident(g8,g7)
    c: Tangent(g17,g8) = -1.5708
    c: Tangent(g17,g3) = 1.5708
    c: Radius(g17) = 2
    c: Tangent(g12,g9) = -1.5708
    c: Tangent(g15,g9) = -1.5708
    c: Tangent(g11,g10) = -1.5708
    c: Coincident(g18,g5)
    c: Horizontal(g18)
    c: Coincident(g18,g6)
    c: Coincident(g10,g5)
    c: Tangent(g13,g18) = 1.5708
    c: Tangent(g14,g18) = 1.5708
    c: Equal(g11,g12)
    c: Equal(g14,g17)
    c: Equal(g17,g16)
    c: Coincident(g19,g11)
    c: Coincident(g19,g4)
    c: Coincident(g20,g15)
    c: Coincident(g20,g12)
    c: Coincident(g21,g14)
    c: Coincident(g21,g13)
    c: Coincident(g22,g17)
    c: Coincident(g22,g16)
    c: Tangent(g26,g27) = 1.5708
    c: Coincident(g30,g24)
    c: Coincident(g31,g32)
    c: Coincident(g33,g31)
    c: Horizontal(g31)
    c: Vertical(g32)
    c: Vertical(g33)
    c: Coincident(g31,g26)
    c: Coincident(g32,g29)
    c: Coincident(g23,g28)
    c: Symmetric(g26,g29,g25)
    c: Tangent(g28,g34) = 1.5708
    c: Tangent(g29,g35) = 1.5708
    c: Tangent(g28,g36) = 1.5708
    c: Tangent(g29,g37) = 1.5708
    c: Tangent(g30,g38) = 1.5708
    c: Tangent(g30,g39) = 1.5708
    c: Equal(g26,g28)
    c: Equal(g28,g29)
    c: Equal(g29,g30)
    c: Radius(g26) = 10
    c: Equal(g27,g36)
    c: Equal(g36,g34)
    c: Equal(g34,g37)
    c: Equal(g35,g38)
    c: Tangent(g39,g31) = -1.5708
    c: Tangent(g27,g33) = -1.5708
    c: Coincident(g31,g30)
    c: Tangent(g40,g31) = -1.5708
    c: Tangent(g40,g26) = 1.5708
    c: Radius(g40) = 2
    c: Tangent(g35,g32) = -1.5708
    c: Tangent(g38,g32) = -1.5708
    c: Tangent(g34,g33) = -1.5708
    c: Coincident(g41,g28)
    c: Horizontal(g41)
    c: Coincident(g41,g29)
    c: Coincident(g33,g28)
    c: Tangent(g36,g41) = 1.5708
    c: Tangent(g37,g41) = 1.5708
    c: Equal(g34,g35)
    c: Equal(g37,g40)
    c: Equal(g40,g39)
    c: Coincident(g42,g34)
    c: Coincident(g42,g27)
    c: Coincident(g43,g38)
    c: Coincident(g43,g35)
    c: Coincident(g44,g37)
    c: Coincident(g44,g36)
    c: Coincident(g45,g40)
    c: Coincident(g45,g39)
    c: Symmetric(g28,g30,g2)
    c: Coincident(g34,g-3)
    c: Coincident(g38,g-4)
    c: DistanceX(g27,g4) = 1
    c: DistanceY(g40,g17) = 1
FEATURE [PartDesign::Pad] Pad004
  BaseFeature = -> Hole
  Direction = (0,0,-1)
  Length = 10
  Length2 = 10
  Profile = -> Sketch013
  ReferenceAxis = -> Sketch013 [N_Axis]
  Reversed = true
  Type = 0
FEATURE [PartDesign::CoordinateSystem] LCS_1
  AttacherType = Attacher::AttachEngine3D
  MapMode = 5
  Support = -> [Pad004]
FEATURE [PartDesign::CoordinateSystem] LCS_2
  AttacherType = Attacher::AttachEngine3D
  AttachmentOffset = pos=(0,0,0) rot=(1,0,0;3.14159rad)
  MapMode = 5
  Support = -> [Pocket]
FEATURE [PartDesign::CoordinateSystem] LCS_3
  AttacherType = Attacher::AttachEngine3D
  MapMode = 2
  Support = -> [Pocket]
FEATURE [PartDesign::Line] HoleAxis_1
  AttacherType = Attacher::AttachEngineLine
  Length = 4.79083
  MapMode = 19
  Placement = pos=(123.349,6.65148,-4.8) rot=(0,1,0;3.14159rad)
  ResizeMode = 1
  Support = -> [Pad004]
FEATURE [PartDesign::Line] HoleAxis_2
  AttacherType = Attacher::AttachEngineLine
  Length = 4.79083
  MapMode = 19
  Placement = pos=(123.349,78.3485,-4.8) rot=(0,1,0;3.14159rad)
  ResizeMode = 1
  Support = -> [Pad004]
FEATURE [PartDesign::Line] HoleAxis_3
  AttacherType = Attacher::AttachEngineLine
  Length = 4.79083
  MapMode = 19
  Placement = pos=(6.65146,78.3485,-4.8) rot=(0,1,0;3.14159rad)
  ResizeMode = 1
  Support = -> [Pad004]
FEATURE [PartDesign::Line] HoleAxis_4
  AttacherType = Attacher::AttachEngineLine
  Length = 4.79083
  MapMode = 19
  Placement = pos=(6.65146,6.65148,-4.8) rot=(0,1,0;3.14159rad)
  ResizeMode = 1
  Support = -> [Pad004]
FEATURE [PartDesign::Body] Body  label="Base"
  Group = -> [ShapeBinder,Sketch010,Sketch011,Pad003,Pocket005,Sketch012,Hole,Sketch013,Pad004,LCS_1,HoleAxis_1,HoleAxis_2,HoleAxis_3,HoleAxis_4]
  Origin = -> Origin
  Tip = -> Pad004
FEATURE [Sketcher::SketchObject] Sketch008
  ExternalGeometry = -> [Pocket]
  FullyConstrained = true
  MapMode = 5
  Placement = pos=(0,0,16) rot=(1,0,0;3.14159rad)
  Support = -> [Pocket]
  sketch-geometry (11):
    g0: LineSegment StartX=8 StartY=-42.6678 StartZ=0 EndX=28 EndY=-42.6678 EndZ=0
    g1: LineSegment StartX=28 StartY=-42.6678 StartZ=0 EndX=28 EndY=-67.1678 EndZ=0
    g2: LineSegment StartX=28 StartY=-67.1678 StartZ=0 EndX=8 EndY=-67.1678 EndZ=0
    g3: LineSegment StartX=8 StartY=-67.1678 StartZ=0 EndX=8 EndY=-42.6678 EndZ=0
    g4: GeomPoint X=8 Y=-42.6678 Z=0
    g5: GeomPoint X=4 Y=-42.6678 Z=0
    g6: LineSegment StartX=4 StartY=-42.6678 StartZ=0 EndX=8 EndY=-42.6678 EndZ=0
    g7: LineSegment StartX=6 StartY=-26.8322 StartZ=0 EndX=36.5 EndY=-26.8322 EndZ=0
    g8: LineSegment StartX=36.5 StartY=-26.8322 StartZ=0 EndX=36.5 EndY=-37.8322 EndZ=0
    g9: LineSegment StartX=36.5 StartY=-37.8322 StartZ=0 EndX=6 EndY=-37.8322 EndZ=0
    g10: LineSegment StartX=6 StartY=-37.8322 StartZ=0 EndX=6 EndY=-26.8322 EndZ=0
  constraints (29):
    c: Coincident(g0,g1)
    c: Coincident(g1,g2)
    c: Coincident(g2,g3)
    c: Coincident(g3,g0)
    c: Horizontal(g0)
    c: Horizontal(g2)
    c: Vertical(g1)
    c: Vertical(g3)
    c: DistanceX(g0,g0) = 20
    c: Coincident(g6,g5)
    c: Coincident(g6,g4)
    c: Horizontal(g6)
    c: DistanceX(g6,g6) = 4
    c: DistanceY(g3,g3) = 24.5
    c: Coincident(g0,g4)
    c: Coincident(g7,g8)
    c: Coincident(g8,g9)
    c: Coincident(g9,g10)
    c: Coincident(g10,g7)
    c: Horizontal(g7)
    c: Horizontal(g9)
    c: Vertical(g8)
    c: Vertical(g10)
    c: DistanceX(g7,g7) = 30.5
    c: DistanceY(g8,g8) = 11
    c: PointOnObject(g5,g-3)
    c: DistanceX(g-3,g7) = 2
    c: DistanceY(g7,g-3) = 11
    c: DistanceY(g-3,g2) = 2
FEATURE [PartDesign::Pocket] Pocket006
  BaseFeature = -> Pocket
  Direction = (0,0,1)
  Length = 2
  Length2 = 5
  Profile = -> Sketch008
  ReferenceAxis = -> Sketch008 [N_Axis]
  Refine = true
  Type = 0
FEATURE [Sketcher::SketchObject] Sketch007
  ExternalGeometry = -> [Pocket004,Sketch003]
  FullyConstrained = true
  MapMode = 5
  Placement = pos=(0,0,19) rot=(1,0,0;3.14159rad)
  Support = -> [Pocket004]
  sketch-geometry (5):
    g0: Circle CenterX=51.5 CenterY=-59 CenterZ=0 NormalX=0 NormalY=0 NormalZ=1 AngleXU=0 Radius=1.35
    g1: Circle CenterX=78.5 CenterY=-59 CenterZ=0 NormalX=0 NormalY=0 NormalZ=1 AngleXU=0 Radius=1.35
    g2: LineSegment StartX=51.5 StartY=-59 StartZ=0 EndX=78.5 EndY=-59 EndZ=0
    g3: LineSegment StartX=65 StartY=-56 StartZ=0 EndX=65 EndY=-62 EndZ=0
    g4: GeomPoint X=65 Y=-59 Z=0
  constraints (11):
    c: Coincident(g2,g0)
    c: Coincident(g2,g1)
    c: Horizontal(g2)
    c: Equal(g1,g0)
    c: Diameter(g0) = 2.7
    c: DistanceX(g2,g2) = 27
    c: Vertical(g3)
    c: Symmetric(g0,g1,g4)
    c: Symmetric(g3,g3,g4)
    c: Symmetric(g-5,g-5,g3)
    c: PointOnObject(g3,g-6)
FEATURE [PartDesign::Body] Body002  label="Front"
  Group = -> [Box002,Sketch001,Pocket001,Sketch002,Pocket002,Sketch003,Pocket003,Sketch004,Pad,Sketch005,Pocket004,Sketch007,Sketch008,Fillet,Sketch,Pocket,LCS_2,Pocket006]
  Origin = -> Origin002
  Tip = -> Pocket006
FEATURE [App::Part] Part002  label="Front inkl. Fasteners"
  Group = -> [Body002,HeatSet,HeatSet001,HeatSet002,HeatSet003,LCS_3]
  Origin = -> Origin016
FEATURE [App::DocumentObjectGroup] Parts
  Group = -> [Tela_OLed_128x64_v15,Body,Part,Part001,Part002]
FEATURE [Part::FeaturePython] Nut  label="M12-Nut"  # Fasteners workbench fastener (typed FeaturePython)
  Placement = pos=(28.0584,15,16) rot=(-1,0,0;3.14159rad)
  baseObject = -> Body002 [Edge54]
  diameter = 11
  invert = false
  matchOuter = false
  offset = 0
  thread = true
  type = 9
